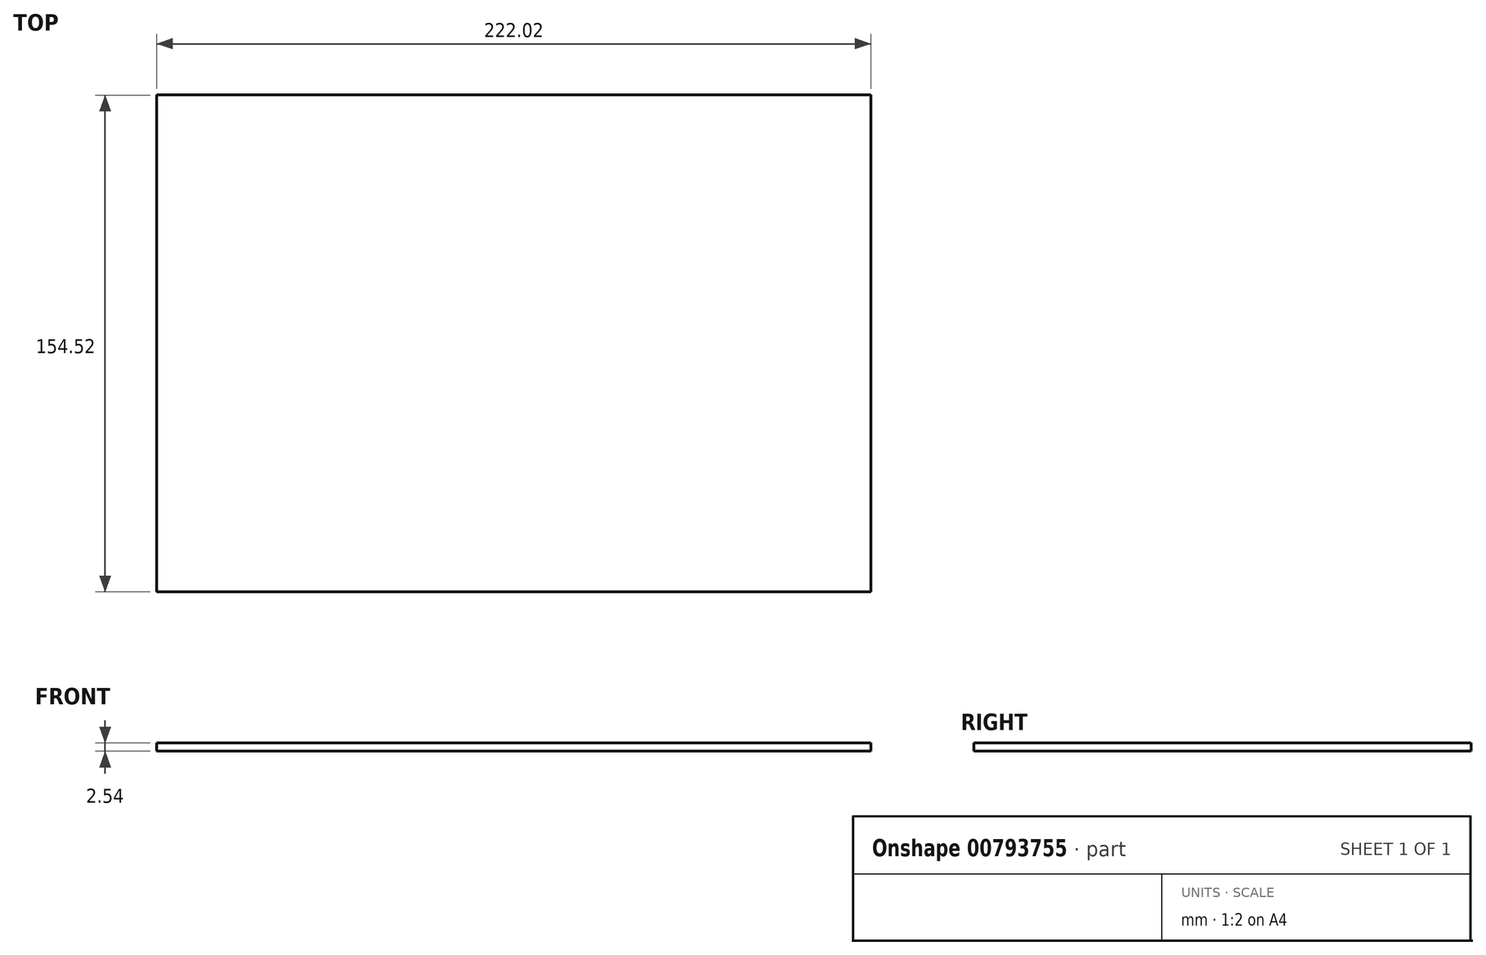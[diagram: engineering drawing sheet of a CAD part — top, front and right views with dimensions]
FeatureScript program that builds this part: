
annotation { "Feature Type Name" : "Feature", "Feature Type Description" : "" }
export const myFeature = defineFeature(function(context is Context, id is Id, definition is map)
    precondition{}
    {
        {
            var Q0;
            Q0=qCreatedBy(makeId("Top.planeOp"),FACE);
            var sketch = newSketch(context, id + "F0", { "sketchPlane" : qUnion([Q0])});
            skLineSegment(sketch, "E0.bottom", {"start": v(-127.5, 77.41) * mm, "end": v(94.52, 77.41) * mm});
            skLineSegment(sketch, "E0.top", {"start": v(-127.5, -77.1) * mm, "end": v(94.52, -77.1) * mm});
            skLineSegment(sketch, "E0.left", {"start": v(-127.5, 77.41) * mm, "end": v(-127.5, -77.1) * mm});
            skLineSegment(sketch, "E0.right", {"start": v(94.52, 77.41) * mm, "end": v(94.52, -77.1) * mm});
            skSolve(sketch);
        }
        {
            var Q0;
            Q0=makeQuery(id+"F0.imprint","IMPRINT",FACE,{"disambiguationData":[TD([[makeQuery(id+"F0.imprint","IMPRINT",EDGE,{"derivedFrom":sQuery(id+"F0.wireOp",EDGE,"E0.bottom")}),-1.0]])]});
            extrude(context, id + "F1", {"entities" : qUnion([Q0]), "depth" : 2.54 * mm, "offsetDistance" : 25.4 * mm});
        }
    });
